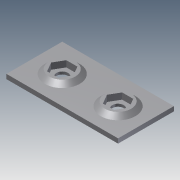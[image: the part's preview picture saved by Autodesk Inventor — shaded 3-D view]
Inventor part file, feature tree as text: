
AUTODESK INVENTOR PART (.ipt)
format: ipt  version: 2011 (Build 150239000, 239)  size: 126,464 bytes
history: native  units: mm
features: extrude x3, sketch x3, draft x1, mirror x1
ambient origin geometry x8: Origin, YZ Plane, XZ Plane, XY Plane, X Axis, Y Axis, Z Axis, Center Point
feature tree (8):
  extrude  "Extrusion4"  Depth=21.5mm
  extrude  "Extrusion5"  Depth=1.75mm TaperAngle=0.0deg
  draft  "FaceDraft2"
  extrude  "Extrusion6"  Depth=1.65mm TaperAngle=0.0deg
  mirror  "Mirror1"
  sketch  "Sketch4"  dims[d12=21.5mm d13=21.5mm]
  sketch  "Sketch5"  dims[d14=4.4mm d15=1.75mm d16=0.0mm]
  sketch  "Sketch6"  dims[d17=13.4mm d18=1.65mm d19=0.0mm d20=45.0deg d21=7.4mm d22=2.4mm d23=0.0mm]
